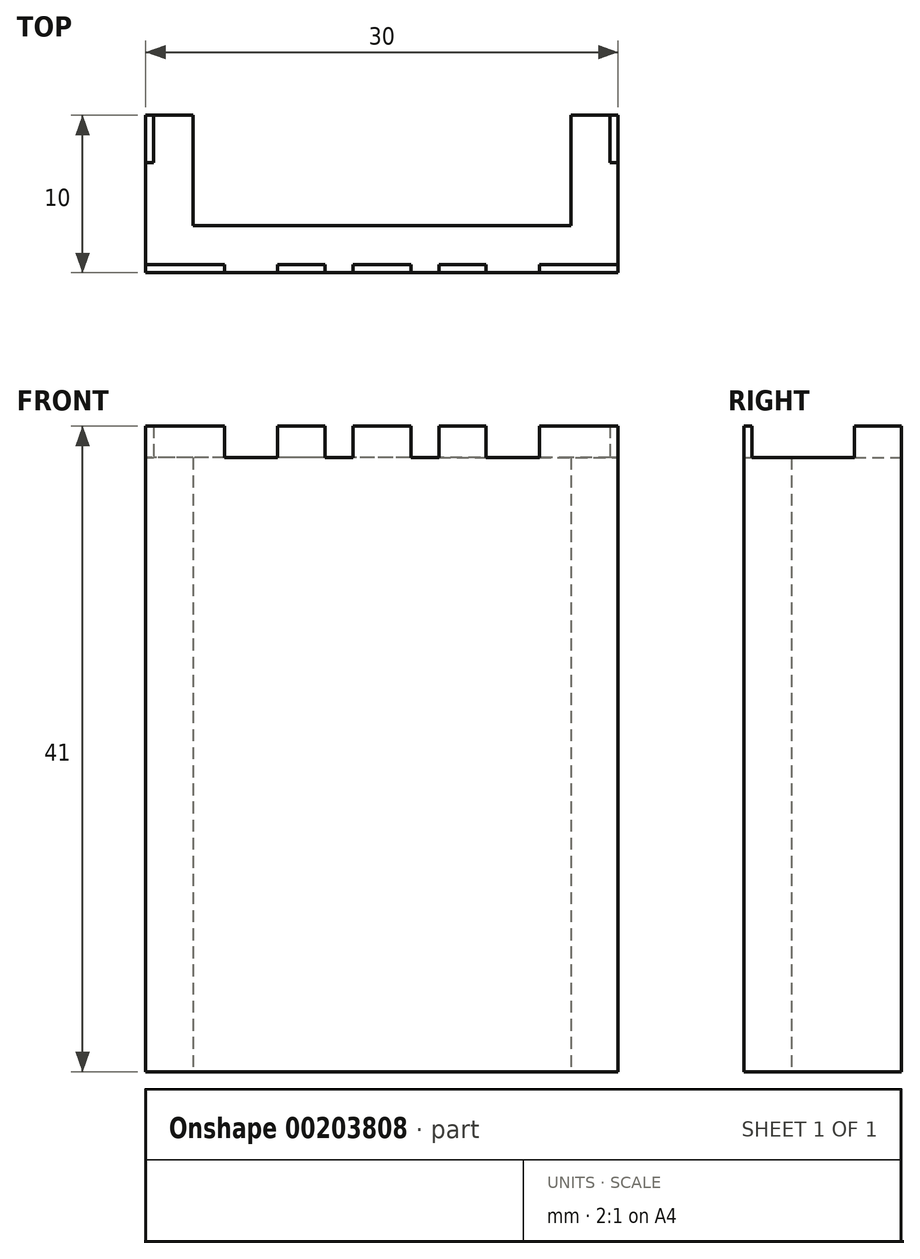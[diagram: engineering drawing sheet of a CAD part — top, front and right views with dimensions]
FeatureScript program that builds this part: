
annotation { "Feature Type Name" : "Feature", "Feature Type Description" : "" }
export const myFeature = defineFeature(function(context is Context, id is Id, definition is map)
    precondition{}
    {
        {
            var Q0;
            Q0=qCreatedBy(makeId("Top.planeOp"),FACE);
            var sketch = newSketch(context, id + "F0", { "sketchPlane" : qUnion([Q0])});
            skLineSegment(sketch, "E0", {"start": v(0, 0) * mm, "end": v(15, 0) * mm});
            skLineSegment(sketch, "E1", {"start": v(15, 0) * mm, "end": v(15, 10) * mm});
            skLineSegment(sketch, "E2", {"start": v(15, 10) * mm, "end": v(12, 10) * mm});
            skLineSegment(sketch, "E3", {"start": v(12, 10) * mm, "end": v(12, 3) * mm});
            skLineSegment(sketch, "E4", {"start": v(12, 3) * mm, "end": v(-12, 3) * mm});
            skLineSegment(sketch, "E5", {"start": v(-12, 3) * mm, "end": v(-12, 10) * mm});
            skLineSegment(sketch, "E6", {"start": v(-12, 10) * mm, "end": v(-15, 10) * mm});
            skLineSegment(sketch, "E7", {"start": v(-15, 10) * mm, "end": v(-15, 0) * mm});
            skLineSegment(sketch, "E8", {"start": v(-15, 0) * mm, "end": v(0, 0) * mm});
            skSolve(sketch);
        }
        {
            var Q0;
            Q0=makeQuery(id+"F0.imprint","IMPRINT",FACE,{"disambiguationData":[TD([[makeQuery(id+"F0.imprint","IMPRINT",EDGE,{"derivedFrom":sQuery(id+"F0.wireOp",EDGE,"E0")}),1.0]])]});
            extrude(context, id + "F1", {"entities" : qUnion([Q0]), "depth" : 39 * mm});
        }
        {
            var Q0;
            Q0=makeQuery(id+"F1.opExtrude","CAP_FACE",FACE,{"disambiguationData":[OSD([sQuery(id+"F0.wireOp",EDGE,"E0"),sQuery(id+"F0.wireOp",EDGE,"E1"),sQuery(id+"F0.wireOp",EDGE,"E2"),sQuery(id+"F0.wireOp",EDGE,"E3"),sQuery(id+"F0.wireOp",EDGE,"E4"),sQuery(id+"F0.wireOp",EDGE,"E5"),sQuery(id+"F0.wireOp",EDGE,"E6"),sQuery(id+"F0.wireOp",EDGE,"E7"),sQuery(id+"F0.wireOp",EDGE,"E8")])],"isStart":false});
            var sketch = newSketch(context, id + "F2", { "sketchPlane" : qUnion([Q0])});
            skLineSegment(sketch, "E9", {"start": v(-15, 10) * mm, "end": v(-15, 7) * mm});
            skLineSegment(sketch, "E10", {"start": v(-15, 7) * mm, "end": v(-14.5, 7) * mm});
            skLineSegment(sketch, "E11", {"start": v(-14.5, 7) * mm, "end": v(-14.5, 10) * mm});
            skLineSegment(sketch, "E12", {"start": v(-14.5, 10) * mm, "end": v(-15, 10) * mm});
            skLineSegment(sketch, "E13.MirrorCS", {"start": v(15, 7) * mm, "end": v(14.5, 7) * mm});
            skLineSegment(sketch, "E14.MirrorCS", {"start": v(14.5, 7) * mm, "end": v(14.5, 10) * mm});
            skLineSegment(sketch, "E15.MirrorCS", {"start": v(14.5, 10) * mm, "end": v(15, 10) * mm});
            skLineSegment(sketch, "E16.MirrorCS", {"start": v(15, 10) * mm, "end": v(15, 7) * mm});
            skLineSegment(sketch, "E17", {"start": v(-15, 0) * mm, "end": v(-10, 0) * mm});
            skLineSegment(sketch, "E18", {"start": v(-10, 0) * mm, "end": v(-10, 0.5) * mm});
            skLineSegment(sketch, "E19", {"start": v(-10, 0.5) * mm, "end": v(-15, 0.5) * mm});
            skLineSegment(sketch, "E20", {"start": v(-15, 0.5) * mm, "end": v(-15, 0) * mm});
            skLineSegment(sketch, "E21", {"start": v(-3.62, 0) * mm, "end": v(-3.62, 0.5) * mm});
            skLineSegment(sketch, "E22", {"start": v(-3.62, 0.5) * mm, "end": v(-6.62, 0.5) * mm});
            skLineSegment(sketch, "E23", {"start": v(-6.62, 0.5) * mm, "end": v(-6.62, 0) * mm});
            skLineSegment(sketch, "E24", {"start": v(-6.62, 0) * mm, "end": v(-3.62, 0) * mm});
            skLineSegment(sketch, "E25.MirrorCS", {"start": v(10, 0) * mm, "end": v(10, 0.5) * mm});
            skLineSegment(sketch, "E26.MirrorCS", {"start": v(3.62, 0) * mm, "end": v(3.62, 0.5) * mm});
            skLineSegment(sketch, "E27.MirrorCS", {"start": v(15, 0.5) * mm, "end": v(15, 0) * mm});
            skLineSegment(sketch, "E28.MirrorCS", {"start": v(6.62, 0.5) * mm, "end": v(6.62, 0) * mm});
            skLineSegment(sketch, "E29.MirrorCS", {"start": v(15, 0) * mm, "end": v(10, 0) * mm});
            skLineSegment(sketch, "E30.MirrorCS", {"start": v(10, 0.5) * mm, "end": v(15, 0.5) * mm});
            skLineSegment(sketch, "E31.MirrorCS", {"start": v(6.62, 0) * mm, "end": v(3.62, 0) * mm});
            skLineSegment(sketch, "E32.MirrorCS", {"start": v(3.62, 0.5) * mm, "end": v(6.62, 0.5) * mm});
            skLineSegment(sketch, "E33", {"start": v(0, 0) * mm, "end": v(-1.84, 0) * mm});
            skLineSegment(sketch, "E34", {"start": v(-1.84, 0) * mm, "end": v(-1.84, 0.5) * mm});
            skLineSegment(sketch, "E35", {"start": v(-1.84, 0.5) * mm, "end": v(0, 0.5) * mm});
            skLineSegment(sketch, "E36.MirrorCS", {"start": v(0, 0) * mm, "end": v(1.84, 0) * mm});
            skLineSegment(sketch, "E37.MirrorCS", {"start": v(1.84, 0.5) * mm, "end": v(0, 0.5) * mm});
            skLineSegment(sketch, "E38.MirrorCS", {"start": v(1.84, 0) * mm, "end": v(1.84, 0.5) * mm});
            skSolve(sketch);
        }
        {
            var Q0;
            Q0=makeQuery(id+"F2.imprint","IMPRINT",FACE,{"disambiguationData":[TD([[makeQuery(id+"F2.imprint","IMPRINT",EDGE,{"derivedFrom":sQuery(id+"F2.wireOp",EDGE,"E9")}),1.0]])]});
            var Q1;
            Q1=makeQuery(id+"F2.imprint","IMPRINT",FACE,{"disambiguationData":[TD([[makeQuery(id+"F2.imprint","IMPRINT",EDGE,{"derivedFrom":sQuery(id+"F2.wireOp",EDGE,"E17")}),1.0]])]});
            var Q2;
            Q2=makeQuery(id+"F2.imprint","IMPRINT",FACE,{"disambiguationData":[TD([[makeQuery(id+"F2.imprint","IMPRINT",EDGE,{"derivedFrom":sQuery(id+"F2.wireOp",EDGE,"E21")}),1.0]])]});
            var Q3;
            Q3=makeQuery(id+"F2.imprint","IMPRINT",FACE,{"disambiguationData":[TD([[makeQuery(id+"F2.imprint","IMPRINT",EDGE,{"derivedFrom":sQuery(id+"F2.wireOp",EDGE,"E33")}),1.0]])]});
            var Q4;
            Q4=makeQuery(id+"F2.imprint","IMPRINT",FACE,{"disambiguationData":[TD([[makeQuery(id+"F2.imprint","IMPRINT",EDGE,{"derivedFrom":sQuery(id+"F2.wireOp",EDGE,"E26.MirrorCS")}),-1.0]])]});
            var Q5;
            Q5=makeQuery(id+"F2.imprint","IMPRINT",FACE,{"disambiguationData":[TD([[makeQuery(id+"F2.imprint","IMPRINT",EDGE,{"derivedFrom":sQuery(id+"F2.wireOp",EDGE,"E25.MirrorCS")}),-1.0]])]});
            var Q6;
            Q6=makeQuery(id+"F2.imprint","IMPRINT",FACE,{"disambiguationData":[TD([[makeQuery(id+"F2.imprint","IMPRINT",EDGE,{"derivedFrom":sQuery(id+"F2.wireOp",EDGE,"E13.MirrorCS")}),-1.0]])]});
            extrude(context, id + "F3", {"entities" : qUnion([Q0, Q1, Q2, Q3, Q4, Q5, Q6]), "operationType" : NewBodyOperationType.ADD, "depth" : 2 * mm});
        }
    });
